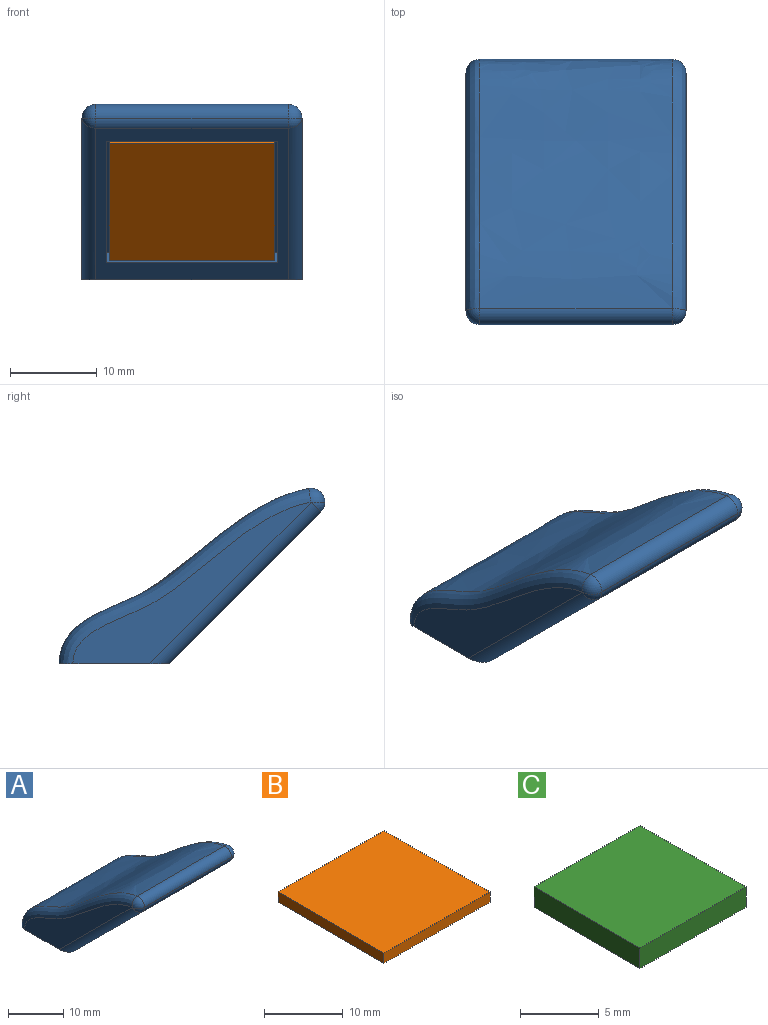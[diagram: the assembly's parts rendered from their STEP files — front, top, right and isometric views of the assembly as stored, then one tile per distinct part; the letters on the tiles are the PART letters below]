
ASSEMBLY  parts=3 mates=2
PART A: 28 faces, bbox 26.1x31.3x22.1 mm
  f0: plane 27.49x18.66mm, normal (1,0,0), area 117mm2, adj f2,f16,f21,f25
  f1: plane 22.23x17.5mm, normal (0,-0.71,-0.71), area 157.4mm2, adj f2,f10,f11,f12,f13,f16,f17,f18
  f2: plane 26.07x13.37mm, normal (0,0,-1), area 196.2mm2, adj f0,f1,f4,f5,f6,f7,f8,f15
  f3: plane 22.23x0.03mm, normal (0,-1,0), area 0.7mm2, adj f17,f21,f22,f23
  f4: plane 27.49x18.66mm, normal (-1,0,0), area 117mm2, adj f2,f18,f22,f27
  f5: plane 11.13x1.59mm, normal (-1,0,0), area 17.7mm2, adj f2,f6,f8,f9
  f6: plane 11.13x1.59mm, normal (0,1,0), area 17.7mm2, adj f2,f5,f7,f9
  f7: plane 11.13x1.59mm, normal (1,0,0), area 17.7mm2, adj f2,f6,f8,f9
  f8: plane 11.13x1.59mm, normal (0,-1,0), area 17.7mm2, adj f2,f5,f7,f9
  f9: plane 11.13x11.13mm, normal (0,0,-1), area 123.8mm2, adj f5,f6,f7,f8
  f10: plane 19.81x1.12mm, normal (0,-0.71,0.71), area 31.5mm2, adj f1,f11,f13,f14
  f11: plane 15.13x15.13mm, normal (-1,0,0), area 31.5mm2, adj f1,f10,f12,f14
  f12: plane 19.81x1.12mm, normal (0,0.71,-0.71), area 31.5mm2, adj f1,f11,f13,f14
  f13: plane 15.13x15.13mm, normal (1,0,0), area 31.5mm2, adj f1,f10,f12,f14
  f14: plane 19.81x14.01mm, normal (0,-0.71,-0.71), area 392.5mm2, adj f10,f11,f12,f13
  f15: extruded ~28.81x22.23mm, area 807mm2, adj f2,f23,f25,f27
  f16: cylinder r=1.59mm len=19.74mm, axis (0,-0.71,0.71), area 63.7mm2, adj f0,f1,f2,f19
  f17: cylinder r=1.59mm len=22.23mm, axis (-1,0,0), area 27.7mm2, adj f1,f3,f19,f20
  f18: cylinder r=1.59mm len=19.74mm, axis (0,0.71,-0.71), area 63.7mm2, adj f1,f2,f4,f20
  f19: sphere r=1.59mm, area 2mm2, adj f16,f17,f21
  f20: sphere r=1.59mm, area 1.5mm2, adj f17,f18,f22
  f21: cylinder r=1.59mm len=1.59mm, axis (0,0,1), area 0.1mm2, adj f0,f3,f19,f24
  f22: cylinder r=1.59mm len=1.59mm, axis (0,0,-1), area 0.1mm2, adj f3,f4,f20,f26
  f23: cylinder r=1.59mm len=22.23mm, axis (-1,0,0), area 61.3mm2, adj f3,f15,f24,f26
  f24: sphere r=1.59mm, area 4.4mm2, adj f21,f23,f25
  f25: bspline ~29.63x20.4mm, area 88.5mm2, adj f0,f2,f15,f24
  f26: sphere r=1.59mm, area 4.4mm2, adj f22,f23,f27
  f27: bspline ~29.63x20.4mm, area 88.5mm2, adj f2,f4,f15,f26
PART B: 6 faces, bbox 19.1x19.1x1.6 mm
  f0: plane 19.05x1.59mm, normal (0,-1,0), area 30.2mm2, adj f1,f3,f4,f5
  f1: plane 19.05x1.59mm, normal (1,0,0), area 30.2mm2, adj f0,f2,f4,f5
  f2: plane 19.05x1.59mm, normal (0,1,0), area 30.2mm2, adj f1,f3,f4,f5
  f3: plane 19.05x1.59mm, normal (-1,0,0), area 30.2mm2, adj f0,f2,f4,f5
  f4: plane 19.05x19.05mm, normal (0,0,1), area 362.9mm2, adj f0,f1,f2,f3
  f5: plane 19.05x19.05mm, normal (0,0,-1), area 362.9mm2, adj f0,f1,f2,f3
PART C: 6 faces, bbox 9.5x9.5x1.6 mm
  f0: plane 9.53x1.59mm, normal (0,-1,0), area 15.1mm2, adj f1,f3,f4,f5
  f1: plane 9.53x1.59mm, normal (1,0,0), area 15.1mm2, adj f0,f2,f4,f5
  f2: plane 9.53x1.59mm, normal (0,1,0), area 15.1mm2, adj f1,f3,f4,f5
  f3: plane 9.53x1.59mm, normal (-1,0,0), area 15.1mm2, adj f0,f2,f4,f5
  f4: plane 9.53x9.53mm, normal (0,0,1), area 90.7mm2, adj f0,f1,f2,f3
  f5: plane 9.53x9.53mm, normal (0,0,-1), area 90.7mm2, adj f0,f1,f2,f3
PLACE A t=(-12.56,-0.05,-0.13)mm
PLACE B rot(axis=(-1,0,0),45deg) t=(0.14,-6.4,-1.34)mm
PLACE C t=(0.14,8.93,-10.32)mm
MATE fastened C.f4 <-> A.f9  axis (0,0,1) through (0.14,8.93,-8.73)mm
MATE fastened B.f4 <-> A.f14  axis (0,0.71,0.71) through (0.14,-5.28,-0.22)mm
